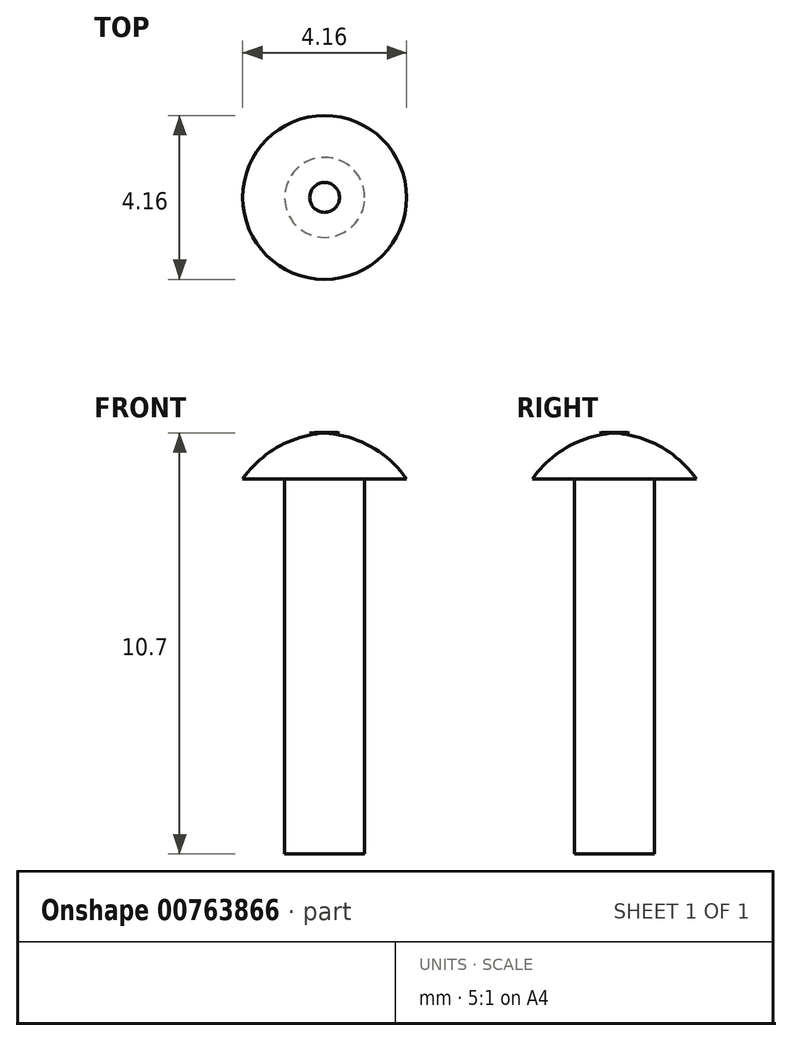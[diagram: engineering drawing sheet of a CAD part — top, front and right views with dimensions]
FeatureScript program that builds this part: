
annotation { "Feature Type Name" : "Feature", "Feature Type Description" : "" }
export const myFeature = defineFeature(function(context is Context, id is Id, definition is map)
    precondition{}
    {
        {
            var Q0;
            Q0=qCreatedBy(makeId("Top.planeOp"),FACE);
            var sketch = newSketch(context, id + "F0", { "sketchPlane" : qUnion([Q0])});
            skCircle(sketch, "E0", {"center": v(0, 0) * mm, "radius": 1.02 * mm});
            skSolve(sketch);
        }
        {
            var Q0;
            Q0 = qSketchRegion(id + "F0", true);
            extrude(context, id + "F1", {"entities" : qUnion([Q0]), "oppositeDirection" : true, "depth" : 9.52 * mm, "offsetDistance" : 25.4 * mm});
        }
        {
            var Q0;
            Q0=qCreatedBy(makeId("Front.planeOp"),FACE);
            var sketch = newSketch(context, id + "F2", { "sketchPlane" : qUnion([Q0])});
            skLineSegment(sketch, "E1", {"start": v(0, 0) * mm, "end": v(-2.08, 0) * mm});
            skLineSegment(sketch, "E2", {"start": v(0, 0) * mm, "end": v(0, 1.17) * mm});
            skArc(sketch, "E3", {"start": v(0, 1.17) * mm, "mid": v(-1.17, 0.82) * mm, "end": v(-2.08, 0) * mm});
            skSolve(sketch);
        }
        {
            var Q0;
            Q0=makeQuery(id+"F2.imprint","IMPRINT",FACE,{"disambiguationData":[TD([[makeQuery(id+"F2.imprint","IMPRINT",EDGE,{"derivedFrom":sQuery(id+"F2.wireOp",EDGE,"E1")}),-1.0]])]});
            var Q1;
            Q1=sQuery(id+"F2.wireOp",EDGE,"E2");
            revolve(context, id + "F3", {"operationType" : NewBodyOperationType.ADD, "surfaceOperationType" : NewSurfaceOperationType.NEW, "entities" : qUnion([Q0]), "axis" : qUnion([Q1]), "revolveType" : RevolveType.FULL});
        }
    });
